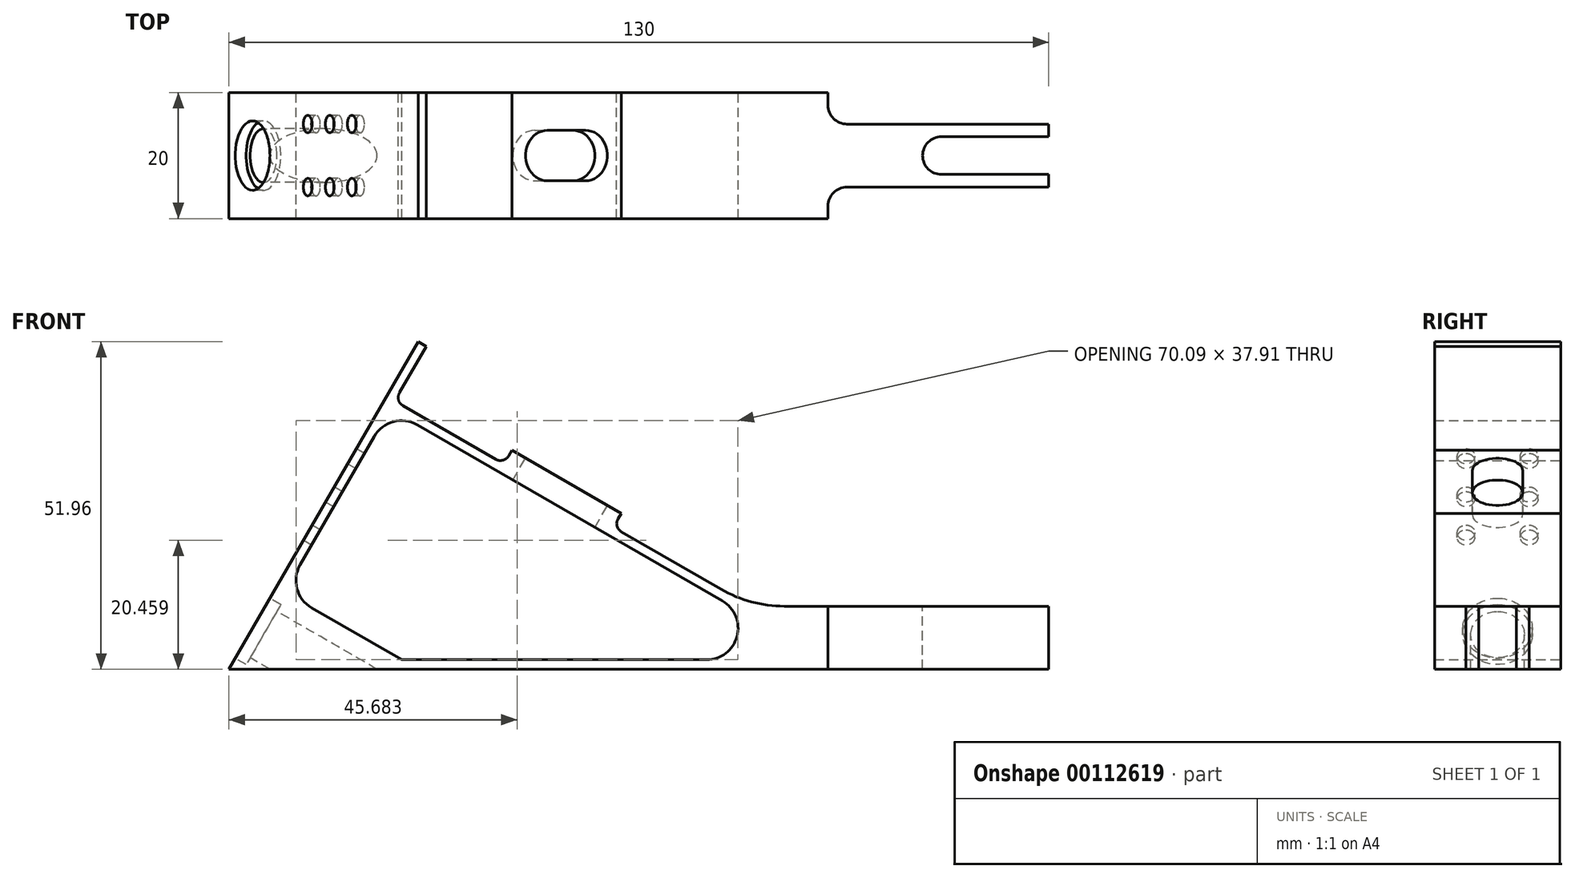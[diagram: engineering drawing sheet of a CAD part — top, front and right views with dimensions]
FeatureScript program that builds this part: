
annotation { "Feature Type Name" : "Feature", "Feature Type Description" : "" }
export const myFeature = defineFeature(function(context is Context, id is Id, definition is map)
    precondition{}
    {
        {
            var Q0;
            Q0=qCreatedBy(makeId("Front.planeOp"),FACE);
            var sketch = newSketch(context, id + "F0", { "sketchPlane" : qUnion([Q0])});
            skLineSegment(sketch, "E0", {"start": v(-30.98, -10.83) * mm, "end": v(99.02, -10.83) * mm});
            skLineSegment(sketch, "E1", {"start": v(99.02, -10.83) * mm, "end": v(99.02, -0.83) * mm});
            skLineSegment(sketch, "E2", {"start": v(-30.98, -10.83) * mm, "end": v(-0.98, 41.13) * mm});
            skLineSegment(sketch, "E3", {"start": v(-0.98, 41.13) * mm, "end": v(0.32, 40.38) * mm});
            skLineSegment(sketch, "E4", {"start": v(0.32, 40.38) * mm, "end": v(-3.93, 33.02) * mm});
            skLineSegment(sketch, "E5", {"start": v(-3.38, 30.97) * mm, "end": v(11.34, 22.47) * mm});
            skLineSegment(sketch, "E6", {"start": v(13.39, 23.02) * mm, "end": v(13.89, 23.89) * mm});
            skLineSegment(sketch, "E7", {"start": v(13.89, 23.89) * mm, "end": v(31.2, 13.89) * mm});
            skLineSegment(sketch, "E8", {"start": v(31.2, 13.89) * mm, "end": v(30.7, 13.02) * mm});
            skLineSegment(sketch, "E9", {"start": v(31.26, 10.97) * mm, "end": v(47.06, 1.85) * mm});
            skLineSegment(sketch, "E10", {"start": v(99.02, -0.83) * mm, "end": v(57.06, -0.83) * mm});
            skArc(sketch, "E11", {"start": v(47.06, 1.85) * mm, "mid": v(51.88, -0.15) * mm, "end": v(57.06, -0.83) * mm});
            skPoint(sketch, "E12.visualSharp", {"position": v(-4.68, 31.72) * mm});
            skArc(sketch, "E12.filletArc", {"start": v(-3.93, 33.02) * mm, "mid": v(-4.08, 31.89) * mm, "end": v(-3.38, 30.97) * mm});
            skPoint(sketch, "E13.visualSharp", {"position": v(12.64, 21.72) * mm});
            skArc(sketch, "E13.filletArc", {"start": v(11.34, 22.47) * mm, "mid": v(12.48, 22.32) * mm, "end": v(13.39, 23.02) * mm});
            skPoint(sketch, "E14.visualSharp", {"position": v(29.96, 11.72) * mm});
            skArc(sketch, "E14.filletArc", {"start": v(30.7, 13.02) * mm, "mid": v(30.56, 11.89) * mm, "end": v(31.26, 10.97) * mm});
            skLineSegment(sketch, "E15", {"start": v(-19.68, 5.74) * mm, "end": v(-7.93, 26.1) * mm});
            skLineSegment(sketch, "E16", {"start": v(-17.85, -1.09) * mm, "end": v(-3.58, -9.33) * mm});
            skLineSegment(sketch, "E17", {"start": v(-3.58, -9.33) * mm, "end": v(44.76, -9.33) * mm});
            skArc(sketch, "E18.filletArc", {"start": v(-19.68, 5.74) * mm, "mid": v(-20.18, 1.95) * mm, "end": v(-17.85, -1.09) * mm});
            skLineSegment(sketch, "E19", {"start": v(-1.1, 27.93) * mm, "end": v(47.26, 0) * mm});
            skArc(sketch, "E20.filletArc", {"start": v(-1.1, 27.93) * mm, "mid": v(-4.9, 28.42) * mm, "end": v(-7.93, 26.1) * mm});
            skPoint(sketch, "E21.visualSharp", {"position": v(63.42, -9.33) * mm});
            skArc(sketch, "E21.filletArc", {"start": v(44.76, -9.33) * mm, "mid": v(49.59, -5.62) * mm, "end": v(47.26, 0) * mm});
            skLineSegment(sketch, "E22", {"start": v(64.02, -0.83) * mm, "end": v(64.02, -10.83) * mm});
            skSolve(sketch);
        }
        {
            var Q0;
            Q0 = qSketchRegion(id + "F0", true);
            extrude(context, id + "F1", {"entities" : qUnion([Q0]), "depth" : 20 * mm});
        }
        {
            var Q0;
            Q0=makeQuery(id+"F1.opExtrude","SWEPT_FACE",FACE,{"disambiguationData":[OSD([sQuery(id+"F0.wireOp",EDGE,"E7")])]});
            var sketch = newSketch(context, id + "F2", { "sketchPlane" : qUnion([Q0])});
            skLineSegment(sketch, "E23", {"start": v(6.58, -10) * mm, "end": v(13.58, -10) * mm, "construction": true});
            skPoint(sketch, "E23.startSnap0", {"position": v(0.08, -10) * mm});
            skArc(sketch, "E24", {"start": v(6.58, -6) * mm, "mid": v(2.58, -10) * mm, "end": v(6.58, -14) * mm});
            skArc(sketch, "E25", {"start": v(13.58, -14) * mm, "mid": v(17.58, -10) * mm, "end": v(13.58, -6) * mm});
            skLineSegment(sketch, "E26", {"start": v(6.58, -6) * mm, "end": v(13.58, -6) * mm});
            skLineSegment(sketch, "E27", {"start": v(6.58, -14) * mm, "end": v(13.58, -14) * mm});
            skSolve(sketch);
        }
        {
            var Q0;
            Q0 = qSketchRegion(id + "F2", true);
            extrude(context, id + "F3", {"entities" : qUnion([Q0]), "operationType" : NewBodyOperationType.REMOVE, "oppositeDirection" : true, "depth" : 25 * mm});
        }
        {
            var Q0;
            Q0=makeQuery(id+"F1.opExtrude","SWEPT_FACE",FACE,{"disambiguationData":[OSD([sQuery(id+"F0.wireOp",EDGE,"E10")])]});
            var sketch = newSketch(context, id + "F4", { "sketchPlane" : qUnion([Q0])});
            skLineSegment(sketch, "E28", {"start": v(57.06, 0) * mm, "end": v(64.02, 0) * mm});
            skLineSegment(sketch, "E29", {"start": v(64.02, 0) * mm, "end": v(64.02, -5) * mm});
            skLineSegment(sketch, "E30", {"start": v(64.02, -5) * mm, "end": v(99.02, -5) * mm});
            skLineSegment(sketch, "E31", {"start": v(99.02, -5) * mm, "end": v(99.02, -7) * mm});
            skLineSegment(sketch, "E32", {"start": v(99.02, -7) * mm, "end": v(82.02, -7) * mm});
            skArc(sketch, "E33", {"start": v(82.02, -7) * mm, "mid": v(79.02, -10) * mm, "end": v(82.02, -13) * mm});
            skLineSegment(sketch, "E34", {"start": v(82.02, -13) * mm, "end": v(99.02, -13) * mm});
            skLineSegment(sketch, "E35", {"start": v(99.02, -13) * mm, "end": v(99.02, -15) * mm});
            skLineSegment(sketch, "E36", {"start": v(99.02, -15) * mm, "end": v(64.02, -15) * mm});
            skLineSegment(sketch, "E37", {"start": v(64.02, -15) * mm, "end": v(64.02, -20) * mm});
            skLineSegment(sketch, "E38", {"start": v(99.02, 0) * mm, "end": v(99.02, -20) * mm, "construction": true});
            skLineSegment(sketch, "E39", {"start": v(99.02, -20) * mm, "end": v(99.02, -10) * mm, "construction": true});
            skLineSegment(sketch, "E40", {"start": v(99.02, -10) * mm, "end": v(57.06, -10) * mm, "construction": true});
            skSolve(sketch);
        }
        {
            var Q0;
            Q0=makeQuery(id+"F1.opExtrude","SWEPT_FACE",FACE,{"disambiguationData":[OSD([sQuery(id+"F0.wireOp",EDGE,"E2")])]});
            var sketch = newSketch(context, id + "F5", { "sketchPlane" : qUnion([Q0])});
            skLineSegment(sketch, "E41.0", {"start": v(20, 35.13) * mm, "end": v(0, 35.13) * mm});
            skLineSegment(sketch, "E42", {"start": v(10, 35.13) * mm, "end": v(10, -34.21) * mm, "construction": true});
            skLineSegment(sketch, "E43.0", {"start": v(20, -24.87) * mm, "end": v(0, -24.87) * mm});
            skCircle(sketch, "E44", {"center": v(15, 14.13) * mm, "radius": 1.4 * mm});
            skCircle(sketch, "E45", {"center": v(10, -17.37) * mm, "radius": 4.25 * mm});
            skCircle(sketch, "E46", {"center": v(10, -17.37) * mm, "radius": 5.5 * mm});
            skCircle(sketch, "E47.1.0.0", {"center": v(15, 7.13) * mm, "radius": 1.4 * mm});
            skCircle(sketch, "E47.2.0.0", {"center": v(15, 0.13) * mm, "radius": 1.4 * mm});
            skLineSegment(sketch, "E47.direction1", {"start": v(15, 14.13) * mm, "end": v(15, 7.13) * mm, "construction": true});
            skCircle(sketch, "E48.1.0.0", {"center": v(5, 14.13) * mm, "radius": 1.4 * mm});
            skLineSegment(sketch, "E48.direction1", {"start": v(15, 14.13) * mm, "end": v(5, 14.13) * mm, "construction": true});
            skCircle(sketch, "E49.1.0.0", {"center": v(5, 7.13) * mm, "radius": 1.4 * mm});
            skCircle(sketch, "E49.2.0.0", {"center": v(5, 0.13) * mm, "radius": 1.4 * mm});
            skLineSegment(sketch, "E49.direction1", {"start": v(5, 14.13) * mm, "end": v(5, 7.13) * mm, "construction": true});
            skSolve(sketch);
        }
        {
            var Q0;
            {var subQ0=sQuery(id+"F4.wireOp",EDGE,"E29");Q0=makeQuery(id+"F4.imprint","IMPRINT",FACE,{"disambiguationData":[TD([[makeQuery(id+"F4.imprint","IMPRINT",EDGE,{"derivedFrom":subQ0}),1.0]])]});}
            extrude(context, id + "F6", {"entities" : qUnion([Q0]), "operationType" : NewBodyOperationType.REMOVE, "endBound" : BoundingType.THROUGH_ALL, "oppositeDirection" : true, "depth" : 25 * mm});
        }
        {
            var Q0;
            {var subQ0=sQuery(id+"F4.wireOp",EDGE,"E36");Q0=makeQuery(id+"F4.imprint","IMPRINT",FACE,{"disambiguationData":[TD([[makeQuery(id+"F4.imprint","IMPRINT",EDGE,{"derivedFrom":subQ0}),1.0]])]});}
            extrude(context, id + "F7", {"entities" : qUnion([Q0]), "operationType" : NewBodyOperationType.REMOVE, "endBound" : BoundingType.THROUGH_ALL, "oppositeDirection" : true, "depth" : 25 * mm});
        }
        {
            var Q0;
            {var subQ0=sQuery(id+"F4.wireOp",EDGE,"E32");Q0=makeQuery(id+"F4.imprint","IMPRINT",FACE,{"disambiguationData":[TD([[makeQuery(id+"F4.imprint","IMPRINT",EDGE,{"derivedFrom":subQ0}),1.0]])]});}
            extrude(context, id + "F8", {"entities" : qUnion([Q0]), "operationType" : NewBodyOperationType.REMOVE, "endBound" : BoundingType.THROUGH_ALL, "oppositeDirection" : true, "depth" : 25 * mm});
        }
        {
            var Q0;
            Q0=makeQuery(id+"F6.boolean.opBoolean","COPY",EDGE,{"derivedFrom":makeQuery(id+"F6.opExtrude","SWEPT_EDGE",EDGE,{"disambiguationData":[OSD([sQuery(id+"F4.wireOp",EDGE,"E29"),sQuery(id+"F4.wireOp",EDGE,"E30")])]})});
            var Q1;
            Q1=makeQuery(id+"F7.boolean.opBoolean","COPY",EDGE,{"derivedFrom":makeQuery(id+"F7.opExtrude","SWEPT_EDGE",EDGE,{"disambiguationData":[OSD([sQuery(id+"F4.wireOp",EDGE,"E36"),sQuery(id+"F4.wireOp",EDGE,"E37")])]})});
            fillet(context, id + "F9", {"entities" : qUnion([Q0, Q1]), "radius" : 3 * mm, "tangentPropagation" : true, "allowEdgeOverflow" : false});
        }
        {
            var Q0;
            Q0=makeQuery(id+"F5.imprint","IMPRINT",FACE,{"disambiguationData":[TD([[makeQuery(id+"F5.imprint","IMPRINT",EDGE,{"derivedFrom":sQuery(id+"F5.wireOp",EDGE,"E47.1.0.0")}),1.0]])]});
            var Q1;
            Q1=makeQuery(id+"F5.imprint","IMPRINT",FACE,{"disambiguationData":[TD([[makeQuery(id+"F5.imprint","IMPRINT",EDGE,{"derivedFrom":sQuery(id+"F5.wireOp",EDGE,"E44")}),1.0]])]});
            var Q2;
            Q2=makeQuery(id+"F5.imprint","IMPRINT",FACE,{"disambiguationData":[TD([[makeQuery(id+"F5.imprint","IMPRINT",EDGE,{"derivedFrom":sQuery(id+"F5.wireOp",EDGE,"E48.1.0.0")}),1.0]])]});
            var Q3;
            Q3=makeQuery(id+"F5.imprint","IMPRINT",FACE,{"disambiguationData":[TD([[makeQuery(id+"F5.imprint","IMPRINT",EDGE,{"derivedFrom":sQuery(id+"F5.wireOp",EDGE,"E49.1.0.0")}),1.0]])]});
            var Q4;
            Q4=makeQuery(id+"F5.imprint","IMPRINT",FACE,{"disambiguationData":[TD([[makeQuery(id+"F5.imprint","IMPRINT",EDGE,{"derivedFrom":sQuery(id+"F5.wireOp",EDGE,"E49.2.0.0")}),1.0]])]});
            var Q5;
            Q5=makeQuery(id+"F5.imprint","IMPRINT",FACE,{"disambiguationData":[TD([[makeQuery(id+"F5.imprint","IMPRINT",EDGE,{"derivedFrom":sQuery(id+"F5.wireOp",EDGE,"E47.2.0.0")}),1.0]])]});
            extrude(context, id + "F10", {"entities" : qUnion([Q0, Q1, Q2, Q3, Q4, Q5]), "operationType" : NewBodyOperationType.REMOVE, "oppositeDirection" : true, "depth" : 25 * mm});
        }
        {
            var Q0;
            Q0=makeQuery(id+"F5.imprint","IMPRINT",FACE,{"disambiguationData":[TD([[makeQuery(id+"F5.imprint","IMPRINT",EDGE,{"derivedFrom":sQuery(id+"F5.wireOp",EDGE,"E45")}),1.0]])]});
            extrude(context, id + "F11", {"entities" : qUnion([Q0]), "operationType" : NewBodyOperationType.REMOVE, "endBound" : BoundingType.THROUGH_ALL, "oppositeDirection" : true, "depth" : 25 * mm});
        }
        {
            var Q0;
            Q0=makeQuery(id+"F5.imprint","IMPRINT",FACE,{"disambiguationData":[TD([[makeQuery(id+"F5.imprint","IMPRINT",EDGE,{"derivedFrom":sQuery(id+"F5.wireOp",EDGE,"E45")}),-1.0]])]});
            extrude(context, id + "F12", {"entities" : qUnion([Q0]), "operationType" : NewBodyOperationType.REMOVE, "oppositeDirection" : true, "depth" : 2 * mm});
        }
    });
